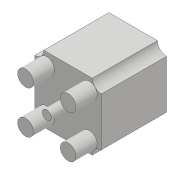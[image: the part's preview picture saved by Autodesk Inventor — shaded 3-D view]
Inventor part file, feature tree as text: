
AUTODESK INVENTOR PART (.ipt)
format: ipt  version: 2018 (Build 220112000, 112)  size: 153,600 bytes
history: native  units: mm
features: extrude x4, sketch x4, projected_geometry x2
ambient origin geometry x8: Origin, YZ Plane, XZ Plane, XY Plane, X Axis, Y Axis, Z Axis, Center Point
bodies: Solid1 (feature_tree)
feature tree (10):
  extrude  "Extrusion1"  Depth=22.0mm
  extrude  "Extrusion2"  Depth=28.5mm
  extrude  "Extrusion3"  Depth=14.5mm
  extrude  "Extrusion4"  Depth=7.0mm
  sketch  "Sketch1"  dims[d0=22.0mm d1=22.0mm]
  sketch  "Sketch2"  dims[d2=28.5mm d3=0.0mm d4=18.0mm]
  sketch  "Sketch3"  dims[d5=14.5mm d6=0.0mm d7=6.0mm]
  projected_geometry  "Projected Loop1"
  sketch  "Sketch4"  dims[d8=6.0mm d9=6.0mm d10=6.0mm d11=10.0mm d12=0.0mm d13=3.0mm d14=16.0mm d15=14.080404mm d16=5.2mm d17=5.2mm d18=5.2mm d19=5.2mm d20=14.080404mm d21=7.0mm d22=0.0mm]
  projected_geometry  "Projected Loop2"
